# Revit family: QF_Hubbell_J6_1-18_cat
name_source: partatom
category: Specialty Equipment
revit_build: Autodesk Revit MEP 2012 (Build: 20110916_2132(x64)
units: mm (PartAtom-declared; Revit-internal decimal feet)

## types (1)
- QF_Hubbell_J6_1-18_cat
    Apparent Power = 1200 VA
    Assembly Code = E1090320
    Box Depth = 1' - 9"
    CSI MasterFormat = 11 40 00
    Conn Conduit = Yes
    Cycle = 60 Hz
    Description = Electric Booster Heater
    Elec Conn Connection Height = 0' - 7 5/16"
    FL Amps = 10 A
    Foodservice Equipment Identifier = Yes
    Height = 1' - 7 3/4"
    Hot Water Connection Height = 0' - 9 5/16"
    Hot Water Consumption = 0.00 GPM
    Hot Water Flow = 0.00 GPM
    Hot Water Maximum Pressure = 75.00 psi
    Hot Water Minimum Pressure = 20.00 psi
    Hot Water Size = 1"
    Leg Depth Seperation = 1' - 2 1/8"
    Manufacturer = Hubbell
    Min Ckt Ampacity = 10 A
    Model = -
    Overall Depth = 2' - 1"
    Phase = 0
    URL = www.hubbellheaters.com
    Volts = 120 V
    Watts = 1000 W
    Weight in Pounds = 95
    Width = 1' - 1"

## geometry (parser evidence)
native form markers: Blend x13, Sweep x2
no freeform markers — native parametric forms only
